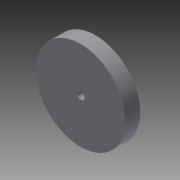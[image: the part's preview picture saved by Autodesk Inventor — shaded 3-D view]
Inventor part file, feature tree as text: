
AUTODESK INVENTOR PART (.ipt)
format: ipt  version: 2015 (Build 190159000, 159)  size: 101,376 bytes
history: native  units: mm
features: extrude x4, sketch x4, plane x1
ambient origin geometry x8: Origin, YZ Plane, XZ Plane, XY Plane, X Axis, Y Axis, Z Axis, Center Point
bodies: Solid1 (feature_tree)
feature tree (9):
  extrude  "Extrusion1"  Depth=5.0mm TaperAngle=0.0deg
  extrude  "Extrusion2"  Depth=10.0mm
  sketch  "Sketch3"  dims[d5=5.0mm d6=0.0mm d7=4.0mm]
  extrude  "Extrusion3"  Depth=5.0mm
  extrude  "Extrusion4"  Depth=3.0mm TaperAngle=0.0deg
  plane  "Work Plane1"
  sketch  "Sketch1"  dims[d0=47.5mm d1=5.0mm d2=0.0mm]
  sketch  "Sketch2"  dims[d3=10.0mm d4=10.0mm]
  sketch  "Sketch4"  dims[d8=5.0mm d9=3.0mm d10=0.0mm d11=3.0mm d12=0.0mm]
